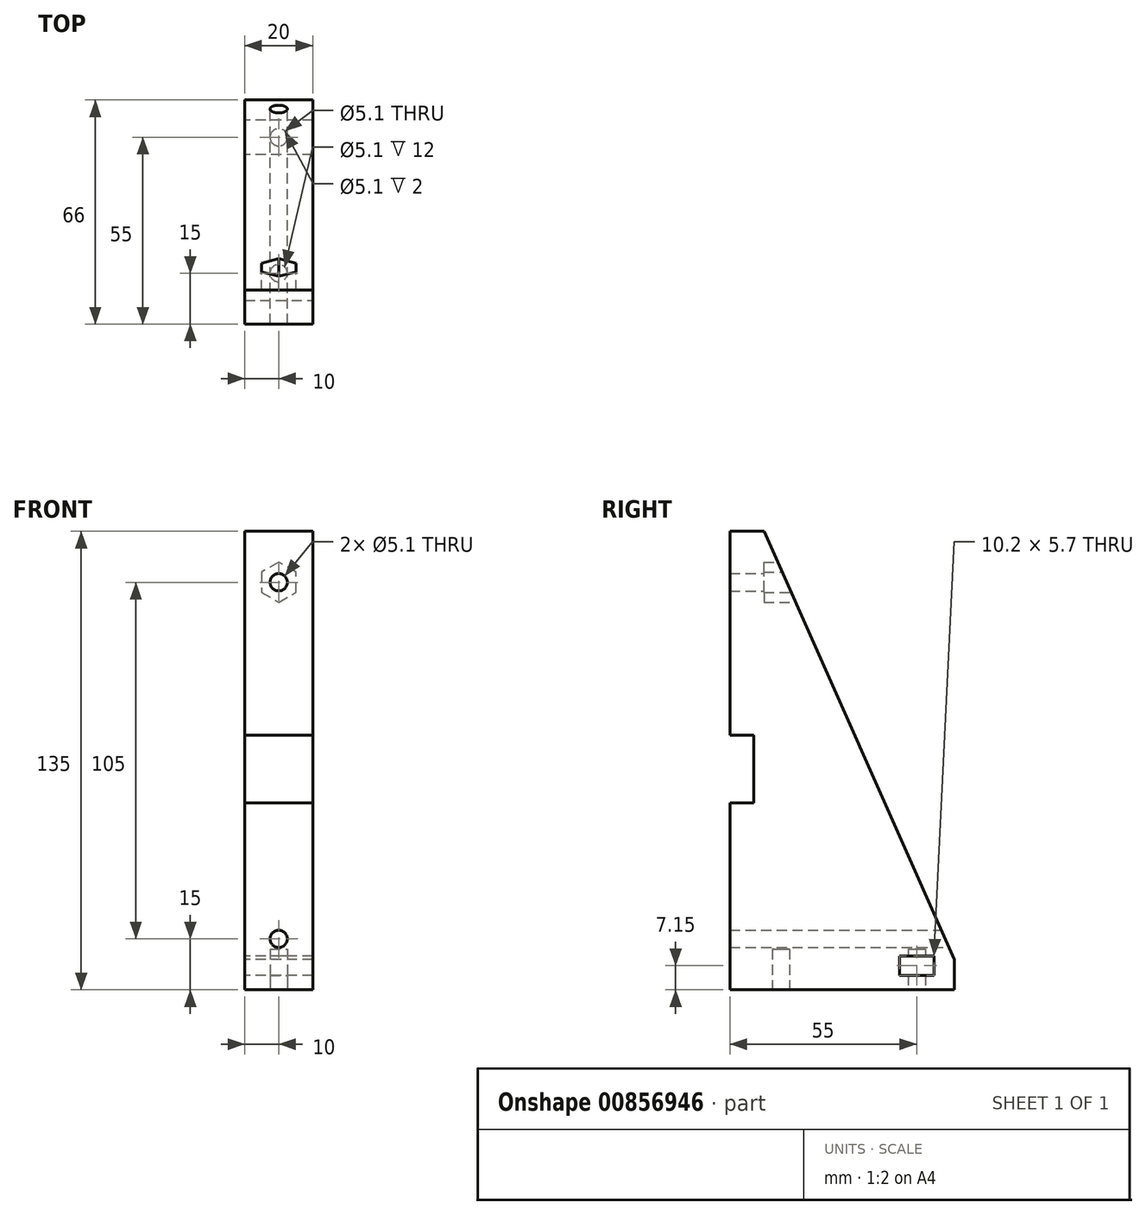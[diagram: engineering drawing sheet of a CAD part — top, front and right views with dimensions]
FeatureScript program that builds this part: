
annotation { "Feature Type Name" : "Feature", "Feature Type Description" : "" }
export const myFeature = defineFeature(function(context is Context, id is Id, definition is map)
    precondition{}
    {
        {
            var Q0;
            Q0=qCreatedBy(makeId("Right.planeOp"),FACE);
            var sketch = newSketch(context, id + "F0", { "sketchPlane" : qUnion([Q0])});
            skLineSegment(sketch, "E0", {"start": v(0, 0) * mm, "end": v(-70, 0) * mm});
            skLineSegment(sketch, "E1", {"start": v(-70, 0) * mm, "end": v(-70, 135) * mm});
            skLineSegment(sketch, "E2", {"start": v(-70, 135) * mm, "end": v(-60, 135) * mm});
            skLineSegment(sketch, "E3", {"start": v(-60, 135) * mm, "end": v(0, 0) * mm});
            skSolve(sketch);
        }
        {
            var Q0;
            Q0=qSketchRegion(id+"F0",true);
            extrude(context, id + "F1", {"entities" : qUnion([Q0]), "depth" : 20 * mm});
        }
        {
            var Q0;
            Q0=makeQuery(id+"F1.opExtrude","SWEPT_FACE",FACE,{"disambiguationData":[OSD([sQuery(id+"F0.wireOp",EDGE,"E1")])]});
            var sketch = newSketch(context, id + "F2", { "sketchPlane" : qUnion([Q0])});
            skLineSegment(sketch, "E4", {"start": v(10, 135) * mm, "end": v(10, 120) * mm});
            skLineSegment(sketch, "E5", {"start": v(10, 0) * mm, "end": v(10, 15) * mm});
            skPoint(sketch, "E6.0.midPoint", {"position": v(16.6, 120) * mm});
            skCircle(sketch, "E7.cCircle", {"center": v(10, 15) * mm, "radius": 5.1 * mm, "construction": true});
            skLineSegment(sketch, "E7.0", {"start": v(4.9, 12.06) * mm, "end": v(4.9, 17.94) * mm});
            skLineSegment(sketch, "E7.1", {"start": v(4.9, 17.94) * mm, "end": v(10, 20.89) * mm});
            skLineSegment(sketch, "E7.2", {"start": v(10, 20.89) * mm, "end": v(15.1, 17.94) * mm});
            skLineSegment(sketch, "E7.3", {"start": v(15.1, 17.94) * mm, "end": v(15.1, 12.06) * mm});
            skLineSegment(sketch, "E7.4", {"start": v(15.1, 12.06) * mm, "end": v(10, 9.11) * mm});
            skLineSegment(sketch, "E7.5", {"start": v(10, 9.11) * mm, "end": v(4.9, 12.06) * mm});
            skPoint(sketch, "E7.0.midPoint", {"position": v(4.9, 15) * mm});
            skCircle(sketch, "E8.cCircle", {"center": v(10, 120) * mm, "radius": 5.1 * mm, "construction": true});
            skLineSegment(sketch, "E8.0", {"start": v(4.9, 117.06) * mm, "end": v(4.9, 122.94) * mm});
            skLineSegment(sketch, "E8.1", {"start": v(4.9, 122.94) * mm, "end": v(10, 125.89) * mm});
            skLineSegment(sketch, "E8.2", {"start": v(10, 125.89) * mm, "end": v(15.1, 122.94) * mm});
            skLineSegment(sketch, "E8.3", {"start": v(15.1, 122.94) * mm, "end": v(15.1, 117.06) * mm});
            skLineSegment(sketch, "E8.4", {"start": v(15.1, 117.06) * mm, "end": v(10, 114.11) * mm});
            skLineSegment(sketch, "E8.5", {"start": v(10, 114.11) * mm, "end": v(4.9, 117.06) * mm});
            skPoint(sketch, "E8.0.midPoint", {"position": v(4.9, 120) * mm});
            skSolve(sketch);
        }
        {
            var Q0;
            Q0=sQuery(id+"F2.wireOp",VERTEX,"E5.end");
            var Q1;
            Q1=sQuery(id+"F2.wireOp",VERTEX,"E4.end");
            var Q2;
            Q2=makeQuery(id+"F1.opExtrude","SWEPT_BODY",BODY,{"disambiguationData":[OSD([sQuery(id+"F0.wireOp",EDGE,"E0"),sQuery(id+"F0.wireOp",EDGE,"E1"),sQuery(id+"F0.wireOp",EDGE,"E2"),sQuery(id+"F0.wireOp",EDGE,"E3")])]});
            hole(context, id + "F3", {"style" : HoleStyle.SIMPLE, "endStyle" : HoleEndStyle.THROUGH, "holeDiameter" : 5.1 * mm, "isTappedThrough" : true, "tappedDepth" : 12 * mm, "tapClearance" : 3, "locations" : qUnion([Q0, Q1]), "scope" : qUnion([Q2]), "startStyle" : HoleStartStyle.PART});
        }
        {
            var Q0;
            Q0=makeQuery(id+"F1.opExtrude","SWEPT_FACE",FACE,{"disambiguationData":[OSD([sQuery(id+"F0.wireOp",EDGE,"E0")])]});
            var sketch = newSketch(context, id + "F4", { "sketchPlane" : qUnion([Q0])});
            skLineSegment(sketch, "E9", {"start": v(10, 70) * mm, "end": v(10, 55) * mm});
            skLineSegment(sketch, "E10", {"start": v(10, 55) * mm, "end": v(10, 15) * mm});
            skPoint(sketch, "E10.endSnap0", {"position": v(10, 0) * mm});
            skCircle(sketch, "E11", {"center": v(10, 55) * mm, "radius": 2.55 * mm});
            skCircle(sketch, "E12", {"center": v(10, 15) * mm, "radius": 2.55 * mm});
            skLineSegment(sketch, "E13", {"start": v(10, 0) * mm, "end": v(10, 4) * mm});
            skLineSegment(sketch, "E14", {"start": v(10, 4) * mm, "end": v(20, 4) * mm});
            skLineSegment(sketch, "E15", {"start": v(20, 4) * mm, "end": v(0, 4) * mm});
            skSolve(sketch);
        }
        {
            var Q0;
            Q0=qSketchRegion(id+"F4",true);
            extrude(context, id + "F5", {"entities" : qUnion([Q0]), "operationType" : NewBodyOperationType.REMOVE, "oppositeDirection" : true, "depth" : 12 * mm});
        }
        {
            var Q0;
            Q0=makeQuery(id+"F2.imprint","IMPRINT",FACE,{"disambiguationData":[TD([[makeQuery(id+"F2.imprint","IMPRINT",EDGE,{"derivedFrom":sQuery(id+"F2.wireOp",EDGE,"E6.0")}),-1.0]])]});
            var Q1;
            Q1=makeQuery(id+"F2.imprint","IMPRINT",FACE,{"disambiguationData":[TD([[makeQuery(id+"F2.imprint","IMPRINT",EDGE,{"derivedFrom":sQuery(id+"F2.wireOp",EDGE,"E8.0")}),-1.0]])]});
            extrude(context, id + "F6", {"entities" : qUnion([Q0, Q1]), "operationType" : NewBodyOperationType.ADD, "oppositeDirection" : true, "depth" : 25 * mm});
        }
        {
            var Q0;
            Q0=makeQuery(id+"F6.opExtrude","CAP_FACE",FACE,{"disambiguationData":[OSD([sQuery(id+"F2.wireOp",EDGE,"E6.0"),sQuery(id+"F2.wireOp",EDGE,"E6.1"),sQuery(id+"F2.wireOp",EDGE,"E6.2"),sQuery(id+"F2.wireOp",EDGE,"E6.3"),sQuery(id+"F2.wireOp",EDGE,"E6.4"),sQuery(id+"F2.wireOp",EDGE,"E6.5")])],"isStart":false});
            var Q1;
            Q1=makeQuery(id+"F6.opExtrude","CAP_FACE",FACE,{"disambiguationData":[OSD([sQuery(id+"F2.wireOp",EDGE,"E8.0"),sQuery(id+"F2.wireOp",EDGE,"E8.1"),sQuery(id+"F2.wireOp",EDGE,"E8.2"),sQuery(id+"F2.wireOp",EDGE,"E8.3"),sQuery(id+"F2.wireOp",EDGE,"E8.4"),sQuery(id+"F2.wireOp",EDGE,"E8.5")])],"isStart":false});
            extrude(context, id + "F7", {"entities" : qUnion([Q0, Q1]), "operationType" : NewBodyOperationType.REMOVE, "oppositeDirection" : true, "depth" : 15 * mm});
        }
        {
            var Q0;
            Q0=sQuery(id+"F2.wireOp",VERTEX,"E4.end");
            var Q1;
            Q1=makeQuery(id+"F1.opExtrude","SWEPT_BODY",BODY,{"disambiguationData":[OSD([sQuery(id+"F0.wireOp",EDGE,"E0"),sQuery(id+"F0.wireOp",EDGE,"E1"),sQuery(id+"F0.wireOp",EDGE,"E2"),sQuery(id+"F0.wireOp",EDGE,"E3")])]});
            hole(context, id + "F8", {"style" : HoleStyle.SIMPLE, "endStyle" : HoleEndStyle.THROUGH, "holeDiameter" : 5.1 * mm, "isTappedThrough" : true, "tappedDepth" : 12 * mm, "tapClearance" : 3, "locations" : qUnion([Q0]), "scope" : qUnion([Q1]), "startStyle" : HoleStartStyle.PART});
        }
        {
            var Q0;
            Q0=makeQuery(id+"F1.opExtrude","CAP_FACE",FACE,{"disambiguationData":[OSD([sQuery(id+"F0.wireOp",EDGE,"E0"),sQuery(id+"F0.wireOp",EDGE,"E1"),sQuery(id+"F0.wireOp",EDGE,"E2"),sQuery(id+"F0.wireOp",EDGE,"E3")])],"isStart":true});
            var sketch = newSketch(context, id + "F9", { "sketchPlane" : qUnion([Q0])});
            skLineSegment(sketch, "E16", {"start": v(0, 0) * mm, "end": v(15, 0) * mm});
            skLineSegment(sketch, "E17", {"start": v(15, 0) * mm, "end": v(15, 10) * mm});
            skLineSegment(sketch, "E18", {"start": v(15, 10) * mm, "end": v(9.9, 10) * mm});
            skLineSegment(sketch, "E19", {"start": v(9.9, 10) * mm, "end": v(9.9, 4.3) * mm});
            skLineSegment(sketch, "E20", {"start": v(9.9, 4.3) * mm, "end": v(20.1, 4.3) * mm});
            skLineSegment(sketch, "E21", {"start": v(20.1, 4.3) * mm, "end": v(20.1, 10) * mm});
            skLineSegment(sketch, "E22", {"start": v(20.1, 10) * mm, "end": v(15, 10) * mm});
            skSolve(sketch);
        }
        {
            var Q0;
            {var subQ0=sQuery(id+"F9.wireOp",EDGE,"E18");Q0=makeQuery(id+"F9.imprint","IMPRINT",FACE,{"disambiguationData":[TD([[makeQuery(id+"F9.imprint","IMPRINT",EDGE,{"derivedFrom":subQ0}),1.0]])]});}
            var Q1;
            {var subQ4=sQuery(id+"F9.wireOp",EDGE,"E21");Q1=makeQuery(id+"F9.imprint","IMPRINT",FACE,{"disambiguationData":[TD([[makeQuery(id+"F9.imprint","IMPRINT",EDGE,{"derivedFrom":subQ4}),1.0]])]});}
            extrude(context, id + "F10", {"entities" : qUnion([Q0, Q1]), "operationType" : NewBodyOperationType.REMOVE, "oppositeDirection" : true, "depth" : 25 * mm});
        }
        {
            var Q0;
            {var subQ0=sQuery(id+"F4.wireOp",EDGE,"E13");Q0=makeQuery(id+"F4.imprint","IMPRINT",FACE,{"disambiguationData":[TD([[makeQuery(id+"F4.imprint","IMPRINT",EDGE,{"derivedFrom":subQ0}),-1.0]])]});}
            var Q1;
            {var subQ0=sQuery(id+"F4.wireOp",EDGE,"E13");Q1=makeQuery(id+"F4.imprint","IMPRINT",FACE,{"disambiguationData":[TD([[makeQuery(id+"F4.imprint","IMPRINT",EDGE,{"derivedFrom":subQ0}),1.0]])]});}
            extrude(context, id + "F11", {"entities" : qUnion([Q0, Q1]), "operationType" : NewBodyOperationType.REMOVE, "oppositeDirection" : true, "depth" : 25 * mm});
        }
        {
            var Q0;
            Q0=makeQuery(id+"F2.imprint","IMPRINT",FACE,{"disambiguationData":[TD([[makeQuery(id+"F2.imprint","IMPRINT",EDGE,{"derivedFrom":sQuery(id+"F2.wireOp",EDGE,"E7.0")}),1.0]])]});
            var sketch = newSketch(context, id + "F12", { "sketchPlane" : qUnion([Q0])});
            skSolve(sketch);
        }
        {
            var Q0;
            Q0=makeQuery(id+"F12.imprint","IMPRINT",FACE,{"disambiguationData":[TD([[makeQuery(id+"F12.imprint","IMPRINT",EDGE,{"derivedFrom":makeQuery(id+"F2.imprint","IMPRINT",EDGE,{"derivedFrom":sQuery(id+"F2.wireOp",EDGE,"E7.0")})}),1.0]])]});
            var sketch = newSketch(context, id + "F13", { "sketchPlane" : qUnion([Q0])});
            skLineSegment(sketch, "E23", {"start": v(0, 0) * mm, "end": v(20, 0) * mm});
            skLineSegment(sketch, "E24", {"start": v(10, 0) * mm, "end": v(10, 55) * mm});
            skLineSegment(sketch, "E25", {"start": v(10, 55) * mm, "end": v(0, 55) * mm});
            skLineSegment(sketch, "E26", {"start": v(0, 55) * mm, "end": v(0, 75) * mm});
            skLineSegment(sketch, "E27", {"start": v(0, 75) * mm, "end": v(20, 75) * mm});
            skLineSegment(sketch, "E28", {"start": v(20, 75) * mm, "end": v(20, 55) * mm});
            skLineSegment(sketch, "E29", {"start": v(20, 55) * mm, "end": v(10, 55) * mm});
            skSolve(sketch);
        }
        {
            var Q0;
            Q0 = qSketchRegion(id + "F13", true);
            extrude(context, id + "F14", {"entities" : qUnion([Q0]), "operationType" : NewBodyOperationType.REMOVE, "oppositeDirection" : true, "depth" : 7 * mm, "offsetDistance" : 25 * mm});
        }
    });
